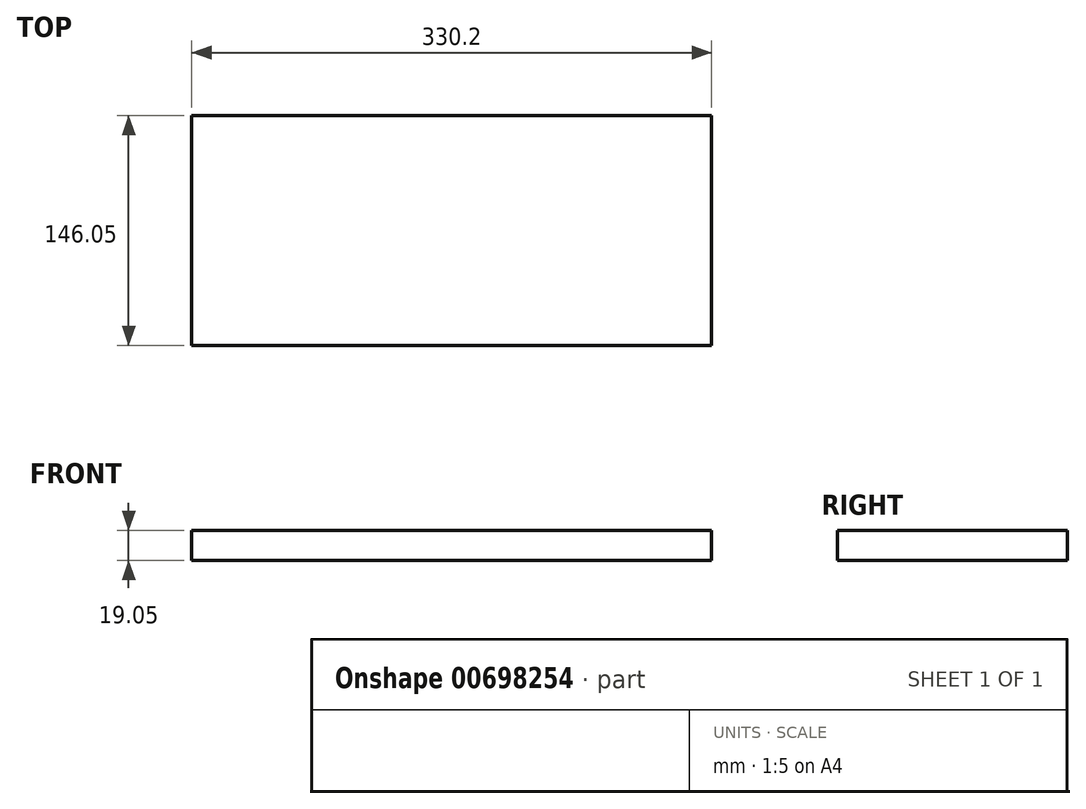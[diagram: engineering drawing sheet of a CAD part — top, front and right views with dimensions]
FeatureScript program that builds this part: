
annotation { "Feature Type Name" : "Feature", "Feature Type Description" : "" }
export const myFeature = defineFeature(function(context is Context, id is Id, definition is map)
    precondition{}
    {
        {
            var Q0;
            Q0=qCreatedBy(makeId("Top.planeOp"),FACE);
            var sketch = newSketch(context, id + "F0", { "sketchPlane" : qUnion([Q0])});
            skLineSegment(sketch, "E0.bottom", {"start": v(-153.76, -132.65) * mm, "end": v(176.44, -132.65) * mm});
            skLineSegment(sketch, "E0.top", {"start": v(-153.76, 13.4) * mm, "end": v(176.44, 13.4) * mm});
            skLineSegment(sketch, "E0.left", {"start": v(-153.76, -132.65) * mm, "end": v(-153.76, 13.4) * mm});
            skLineSegment(sketch, "E0.right", {"start": v(176.44, -132.65) * mm, "end": v(176.44, 13.4) * mm});
            skSolve(sketch);
        }
        {
            var Q0;
            Q0 = qSketchRegion(id + "F0", true);
            extrude(context, id + "F1", {"entities" : qUnion([Q0]), "depth" : 19.05 * mm, "offsetDistance" : 25.4 * mm});
        }
    });
